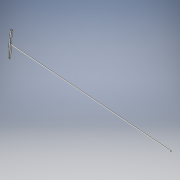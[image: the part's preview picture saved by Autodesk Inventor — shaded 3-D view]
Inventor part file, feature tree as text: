
AUTODESK INVENTOR PART (.ipt)
format: ipt  version: 2018 (Build 220112000, 112)  size: 165,376 bytes
history: native  units: in
note: dims shown in document units (in); Inventor stores cm internally (conversion verified against a paired STEP export)
features: sketch x6, extrude x3, plane x2, sweep x1, other x1, fillet x1, projected_geometry x1
ambient origin geometry x8: Origin, YZ Plane, XZ Plane, XY Plane, X Axis, Y Axis, Z Axis, Center Point
bodies: Solid1 (feature_tree)
feature tree (15):
  extrude  "Extrusion1"  Depth=900.0in
  plane  "Work Plane1"
  extrude  "Extrusion2"  Depth=4.0in
  sketch  "Sketch3"  dims[d5=8.0in d6=0.0in d8=5.0in d9=4.0in]
  plane  "Work Plane2"
  sweep  "Sweep1"
  sketch  "Sketch5"  dims[d13=-4.0in]
  other  "Work Axis1"
  fillet  "Fillet2"  Radius=4.0in
  extrude  "Extrusion3"  Depth=900.0in
  sketch  "Sketch1"  dims[d1=900.0in d2=0.0618in]
  sketch  "Sketch2"  dims[d3=8.0in d4=4.0in]
  sketch  "Sketch4"  dims[d10=5.0in d11=0.0in d12=900.0in]
  projected_geometry  "Projected Loop1"
  sketch  "Sketch6"  dims[d14=0.0in d15=0.0in d16=5.0in d17=1.0in d18=2.5in d19=2.5in d20=3.0in d21=1.0in d22=0.0in]
